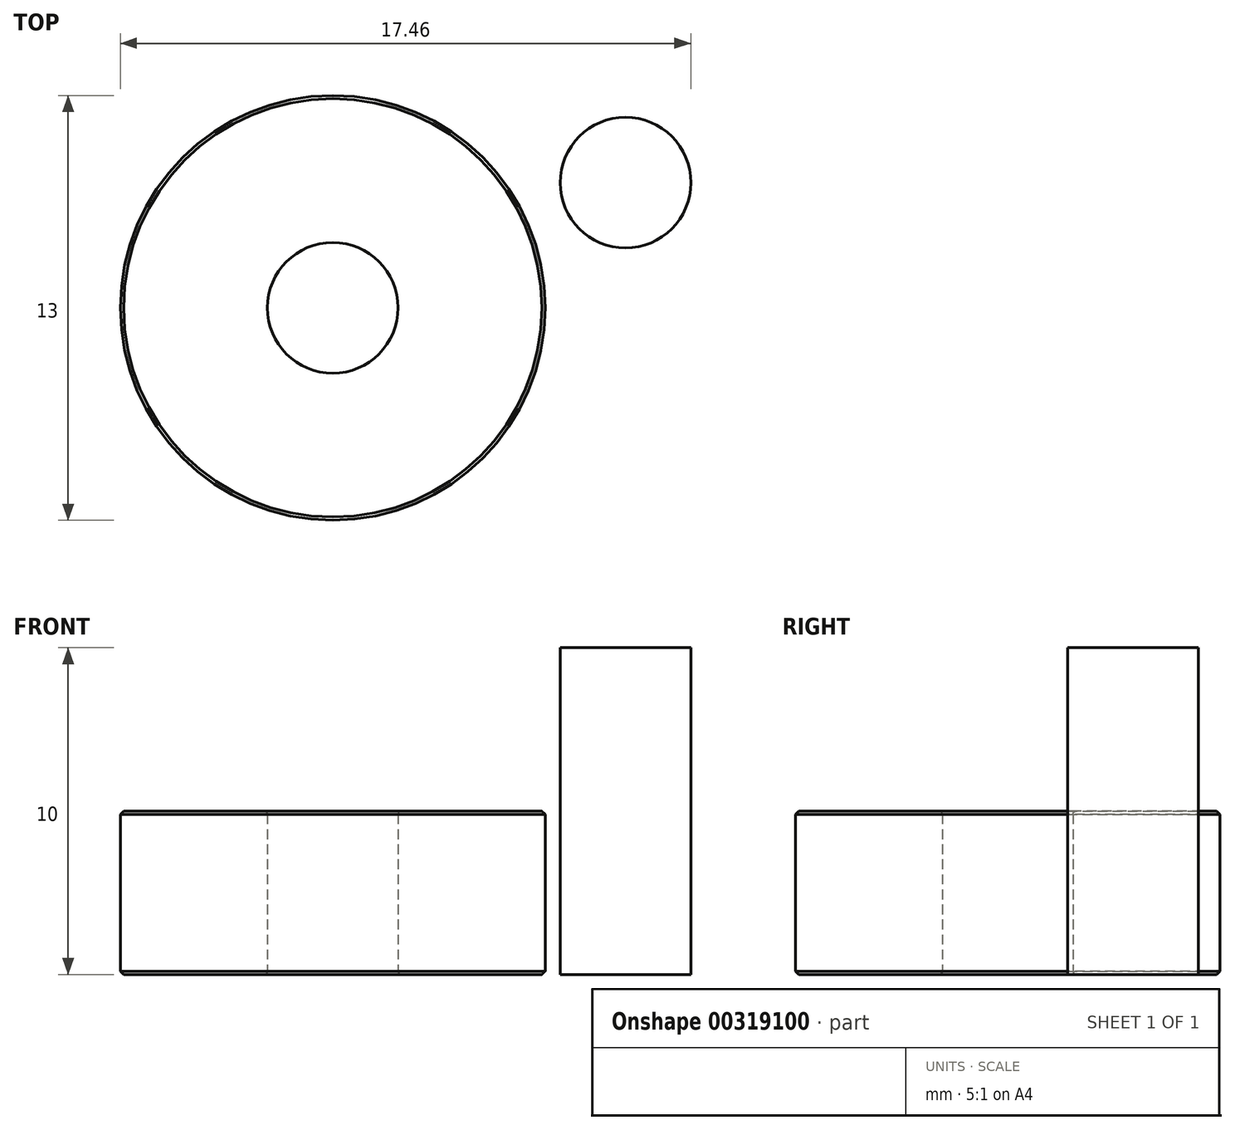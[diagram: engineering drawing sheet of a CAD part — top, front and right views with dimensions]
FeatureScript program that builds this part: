
annotation { "Feature Type Name" : "Feature", "Feature Type Description" : "" }
export const myFeature = defineFeature(function(context is Context, id is Id, definition is map)
    precondition{}
    {
        {
            var Q0;
            Q0=qCreatedBy(makeId("Top.planeOp"),FACE);
            var sketch = newSketch(context, id + "F0", { "sketchPlane" : qUnion([Q0])});
            skCircle(sketch, "E0", {"center": v(0, 0) * mm, "radius": 2 * mm});
            skCircle(sketch, "E1", {"center": v(0, 0) * mm, "radius": 6.5 * mm});
            skSolve(sketch);
        }
        {
            var Q0;
            Q0=makeQuery(id+"F0.imprint","IMPRINT",FACE,{"disambiguationData":[TD([[makeQuery(id+"F0.imprint","IMPRINT",EDGE,{"derivedFrom":sQuery(id+"F0.wireOp",EDGE,"E0")}),-1.0]])]});
            extrude(context, id + "F1", {"entities" : qUnion([Q0]), "depth" : 5 * mm});
        }
        {
            var Q0;
            Q0=makeQuery(id+"F1.opExtrude","CAP_EDGE",EDGE,{"disambiguationData":[OSD([sQuery(id+"F0.wireOp",EDGE,"E1")])],"isStart":false});
            var Q1;
            Q1=makeQuery(id+"F1.opExtrude","CAP_EDGE",EDGE,{"disambiguationData":[OSD([sQuery(id+"F0.wireOp",EDGE,"E1")])],"isStart":true});
            chamfer(context, id + "F2", {"entities" : qUnion([Q0, Q1]), "width" : .1 * mm, "tangentPropagation" : true});
        }
        {
            var Q0;
            Q0=makeQuery(id+"F1.opExtrude","CAP_EDGE",EDGE,{"disambiguationData":[OSD([sQuery(id+"F0.wireOp",EDGE,"E0")])],"isStart":false});
            var Q1;
            Q1=makeQuery(id+"F1.opExtrude","CAP_EDGE",EDGE,{"disambiguationData":[OSD([sQuery(id+"F0.wireOp",EDGE,"E0")])],"isStart":true});
            fillet(context, id + "F3", {"entities" : qUnion([Q0, Q1]), "radius" : .1 * mm, "tangentPropagation" : true, "allowEdgeOverflow" : false});
        }
        {
            var Q0;
            Q0=qCreatedBy(makeId("Top.planeOp"),FACE);
            var sketch = newSketch(context, id + "F4", { "sketchPlane" : qUnion([Q0])});
            skCircle(sketch, "E2", {"center": v(8.96, 3.83) * mm, "radius": 2 * mm});
            skSolve(sketch);
        }
        {
            var Q0;
            Q0=makeQuery(id+"F4.imprint","IMPRINT",FACE,{"disambiguationData":[TD([[makeQuery(id+"F4.imprint","IMPRINT",EDGE,{"derivedFrom":sQuery(id+"F4.wireOp",EDGE,"E2")}),1.0]])]});
            extrude(context, id + "F5", {"entities" : qUnion([Q0]), "depth" : 10 * mm});
        }
    });
